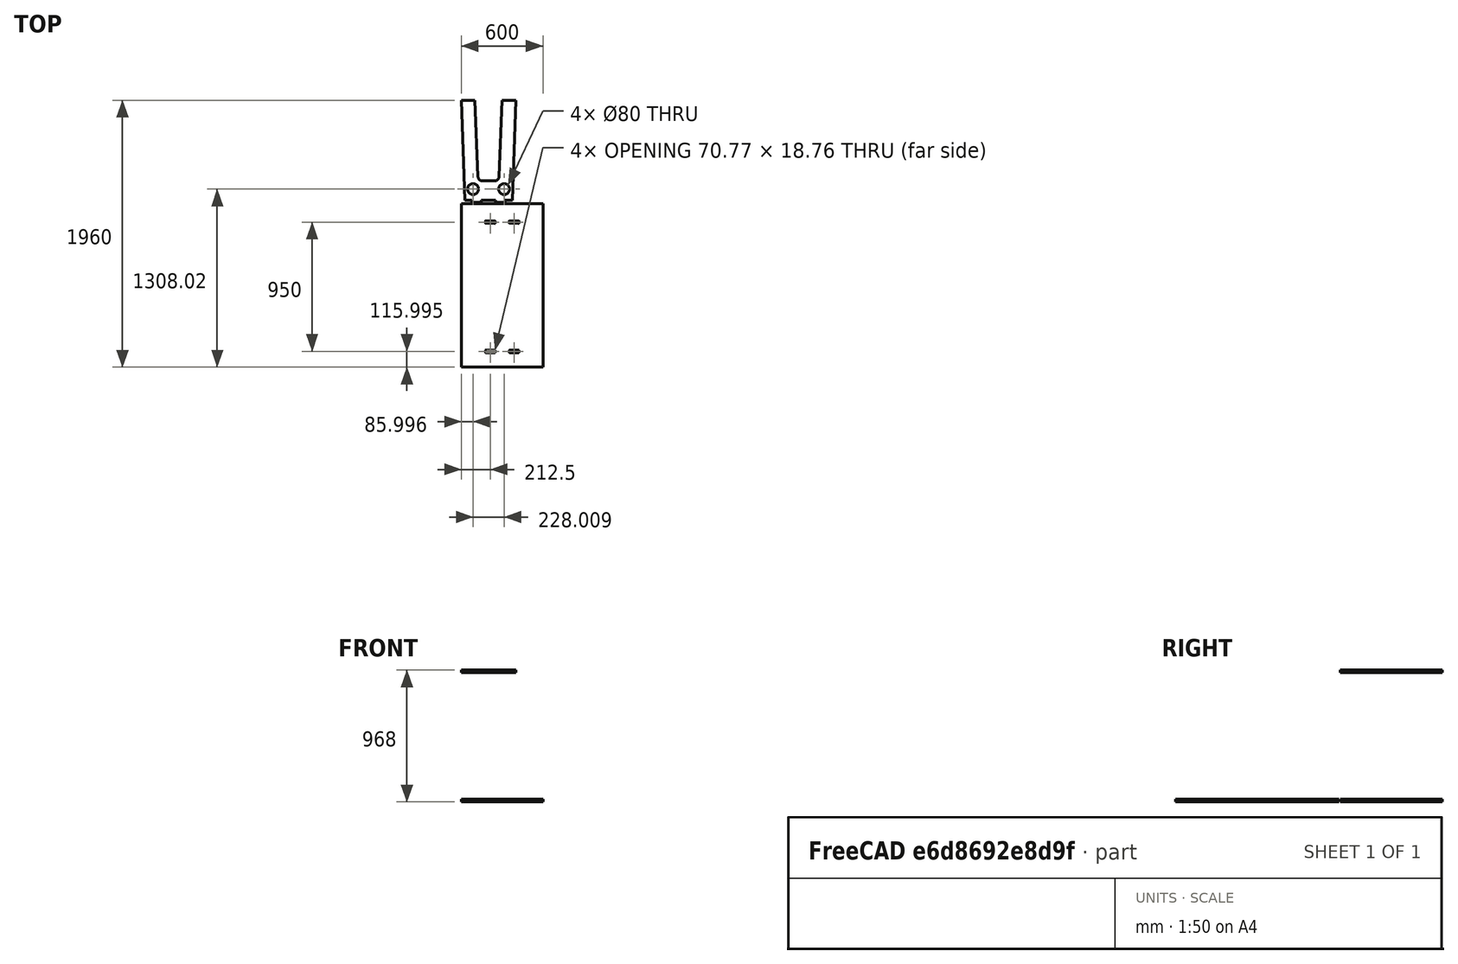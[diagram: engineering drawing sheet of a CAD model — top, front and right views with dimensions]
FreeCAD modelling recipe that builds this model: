
FCSTD DOCUMENT  (FreeCAD 0.16RUnknown)
Label: export
License: All rights reserved
LicenseURL: http://en.wikipedia.org/wiki/All_rights_reserved
objects: Part::Feature×2, Part::Part2DObjectPython×2
note: 4 computed .brp shape members not serialized (recipe doc carries the construction recipe); baked Part::Feature solids carry a one-line shape summary decoded from their .brp

FEATURE [Part::Feature] test
  Placement = pos=(300,600,-702) rot=(0,0,1;0rad)
  shape: bbox 600 x 1200 x 18 mm, 38 faces (baked)
FEATURE [Part::Part2DObjectPython] Shape2DView  # Draft 2D object (typed FeaturePython)
  Base = -> test
  HiddenLines = false
  Projection = (0,0,1)
  ProjectionMode = 0
  SegmentLength = 0.05
  Tessellation = false
FEATURE [Part::Feature] test001
  Placement = pos=(200,1960,523) rot=(1,0,0;1.5708rad)
  shape: bbox 400 x 750 x 968 mm, 44 faces, 2 solids (baked)
FEATURE [Part::Part2DObjectPython] Shape2DView001  # Draft 2D object (typed FeaturePython)
  Base = -> test001
  HiddenLines = false
  Projection = (0,0,1)
  ProjectionMode = 0
  SegmentLength = 0.05
  Tessellation = false
